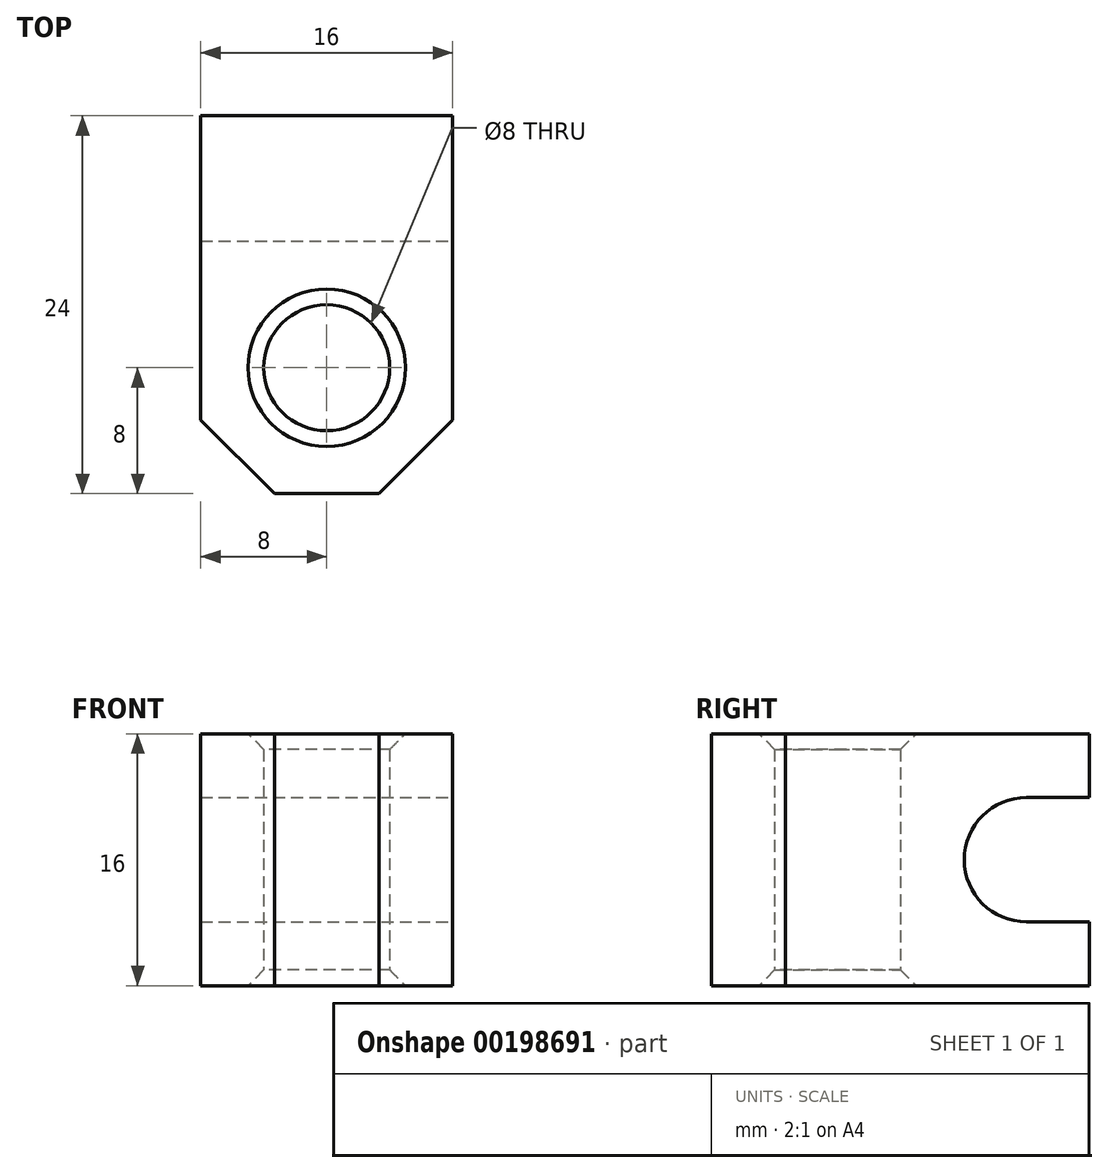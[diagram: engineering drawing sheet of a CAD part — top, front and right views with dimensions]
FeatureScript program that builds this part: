
annotation { "Feature Type Name" : "Feature", "Feature Type Description" : "" }
export const myFeature = defineFeature(function(context is Context, id is Id, definition is map)
    precondition{}
    {
        {
            var Q0;
            Q0=qCreatedBy(makeId("Top.planeOp"),FACE);
            var sketch = newSketch(context, id + "F0", { "sketchPlane" : qUnion([Q0])});
            skCircle(sketch, "E0", {"center": v(0, 0) * mm, "radius": 4 * mm});
            skLineSegment(sketch, "E1", {"start": v(-8, 0) * mm, "end": v(-8, 16) * mm});
            skLineSegment(sketch, "E2", {"start": v(-8, 16) * mm, "end": v(8, 16) * mm});
            skLineSegment(sketch, "E3", {"start": v(8, 16) * mm, "end": v(8, 0) * mm});
            skLineSegment(sketch, "E4", {"start": v(-8, 0) * mm, "end": v(-8, -3.31) * mm});
            skLineSegment(sketch, "E5", {"start": v(-8, -3.31) * mm, "end": v(-3.31, -8) * mm});
            skLineSegment(sketch, "E6", {"start": v(-3.31, -8) * mm, "end": v(3.31, -8) * mm});
            skLineSegment(sketch, "E7", {"start": v(3.31, -8) * mm, "end": v(8, -3.31) * mm});
            skLineSegment(sketch, "E8", {"start": v(8, 0) * mm, "end": v(8, -3.31) * mm});
            skLineSegment(sketch, "E9", {"start": v(0, 0) * mm, "end": v(5.66, -5.66) * mm, "construction": true});
            skPoint(sketch, "E10", {"position": v(2.83, -2.83) * mm});
            skSolve(sketch);
        }
        {
            var Q0;
            Q0=makeQuery(id+"F0.imprint","IMPRINT",FACE,{"disambiguationData":[TD([[makeQuery(id+"F0.imprint","IMPRINT",EDGE,{"derivedFrom":sQuery(id+"F0.wireOp",EDGE,"E0")}),-1.0]])]});
            extrude(context, id + "F1", {"entities" : qUnion([Q0]), "depth" : 16 * mm, "symmetric" : true});
        }
        {
            var Q0;
            Q0=qCreatedBy(makeId("Right.planeOp"),FACE);
            var sketch = newSketch(context, id + "F2", { "sketchPlane" : qUnion([Q0])});
            skLineSegment(sketch, "E11.0", {"start": v(-4, 0) * mm, "end": v(4, 0) * mm, "construction": true});
            skPoint(sketch, "E12.0", {"position": v(16, 0) * mm});
            skArc(sketch, "E13", {"start": v(12, 3.95) * mm, "mid": v(8.05, 0) * mm, "end": v(12, -3.95) * mm});
            skLineSegment(sketch, "E14", {"start": v(12, 3.95) * mm, "end": v(16, 3.95) * mm});
            skLineSegment(sketch, "E15", {"start": v(16, 3.95) * mm, "end": v(16, -3.95) * mm});
            skLineSegment(sketch, "E16", {"start": v(16, -3.95) * mm, "end": v(12, -3.95) * mm});
            skLineSegment(sketch, "E17", {"start": v(4, 0) * mm, "end": v(8.05, 0) * mm, "construction": true});
            skSolve(sketch);
        }
        {
            var Q0;
            Q0 = qSketchRegion(id + "F2", true);
            extrude(context, id + "F3", {"entities" : qUnion([Q0]), "operationType" : NewBodyOperationType.REMOVE, "endBound" : BoundingType.THROUGH_ALL, "oppositeDirection" : true, "depth" : 25 * mm, "hasSecondDirection" : true, "secondDirectionBound" : BoundingType.THROUGH_ALL, "secondDirectionOppositeDirection" : false, "secondDirectionDepth" : 25 * mm});
        }
        {
            var Q0;
            Q0=makeQuery(id+"F1.opExtrude","CAP_EDGE",EDGE,{"disambiguationData":[OSD([sQuery(id+"F0.wireOp",EDGE,"E0")])],"isStart":false});
            var Q1;
            Q1=makeQuery(id+"F1.opExtrude","CAP_EDGE",EDGE,{"disambiguationData":[OSD([sQuery(id+"F0.wireOp",EDGE,"E0")])],"isStart":true});
            chamfer(context, id + "F4", {"entities" : qUnion([Q0, Q1]), "width" : 1 * mm});
        }
    });
